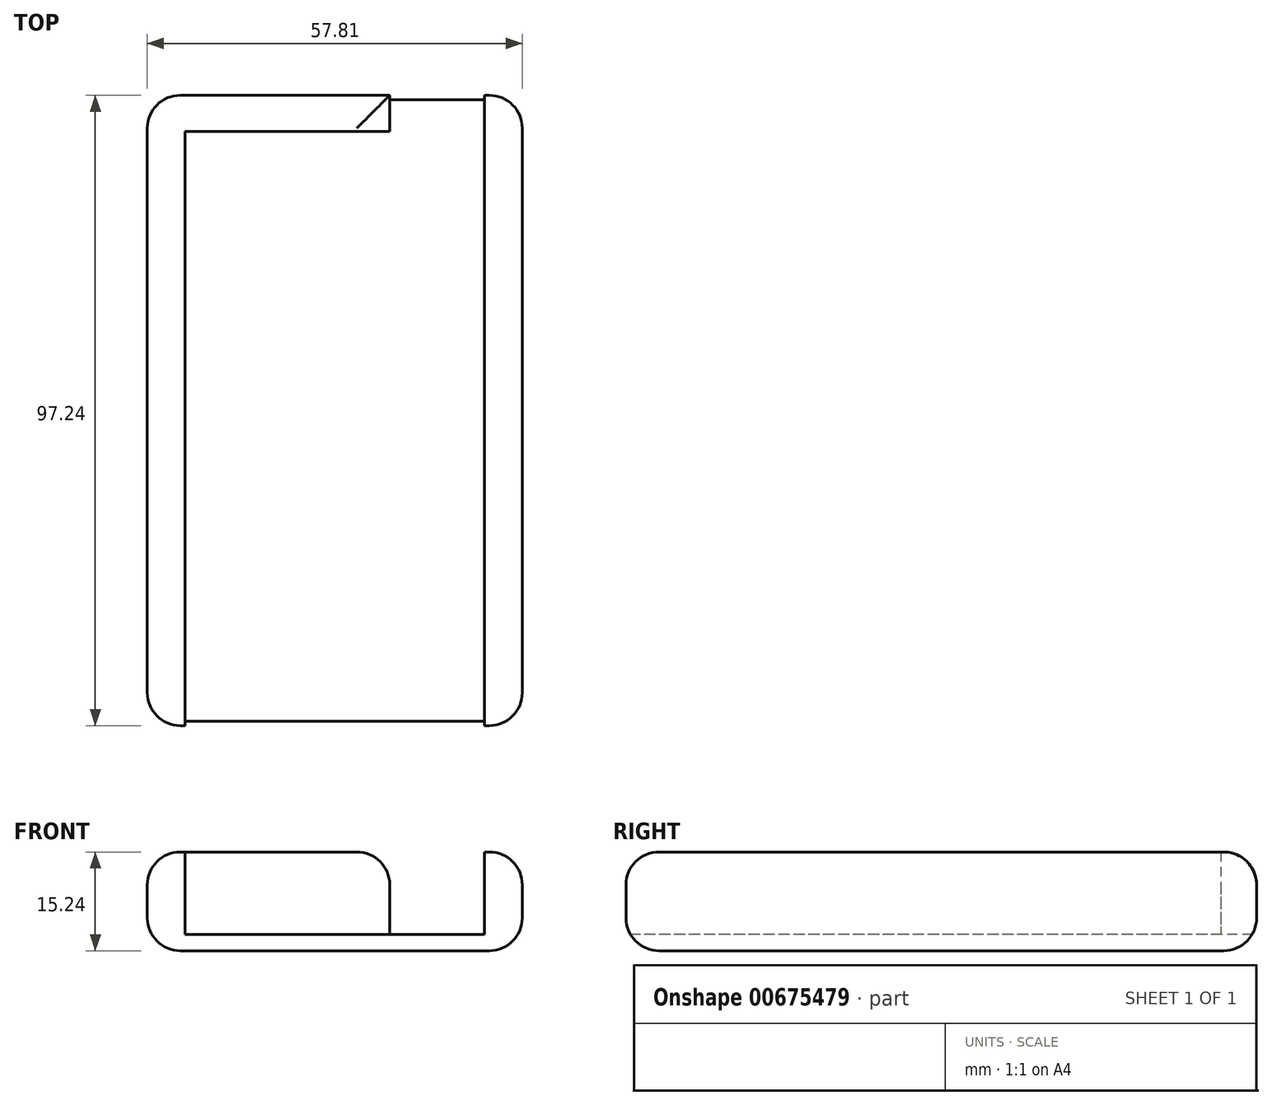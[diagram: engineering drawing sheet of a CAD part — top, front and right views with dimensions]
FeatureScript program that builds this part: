
annotation { "Feature Type Name" : "Feature", "Feature Type Description" : "" }
export const myFeature = defineFeature(function(context is Context, id is Id, definition is map)
    precondition{}
    {
        {
            var Q0;
            Q0=qCreatedBy(makeId("Top.planeOp"),FACE);
            var sketch = newSketch(context, id + "F0", { "sketchPlane" : qUnion([Q0])});
            skLineSegment(sketch, "E0.bottom", {"start": v(-29.05, 48.62) * mm, "end": v(29.05, 48.62) * mm});
            skLineSegment(sketch, "E0.top", {"start": v(-29.05, -48.62) * mm, "end": v(29.05, -48.62) * mm});
            skLineSegment(sketch, "E0.left", {"start": v(-29.05, 48.62) * mm, "end": v(-29.05, -48.62) * mm});
            skLineSegment(sketch, "E0.right", {"start": v(29.05, 48.62) * mm, "end": v(29.05, -48.62) * mm});
            skPoint(sketch, "E0.middle", {"position": v(0, 0) * mm});
            skSolve(sketch);
        }
        {
            var Q0;
            Q0=makeQuery(id+"F0.imprint","IMPRINT",FACE,{"disambiguationData":[TD([[makeQuery(id+"F0.imprint","IMPRINT",EDGE,{"derivedFrom":sQuery(id+"F0.wireOp",EDGE,"E0.bottom")}),-1.0]])]});
            var sketch = newSketch(context, id + "F1", { "sketchPlane" : qUnion([Q0])});
            skLineSegment(sketch, "E1.bottom", {"start": v(-22.92, 48.62) * mm, "end": v(-28.76, 48.62) * mm});
            skLineSegment(sketch, "E1.top", {"start": v(-22.92, -48.91) * mm, "end": v(-28.76, -48.91) * mm});
            skLineSegment(sketch, "E1.left", {"start": v(-22.92, 48.62) * mm, "end": v(-22.92, -48.91) * mm});
            skLineSegment(sketch, "E1.right", {"start": v(-28.76, 48.62) * mm, "end": v(-28.76, -48.91) * mm});
            skLineSegment(sketch, "E2.bottom", {"start": v(29.05, 48.91) * mm, "end": v(23.21, 48.91) * mm});
            skLineSegment(sketch, "E2.top", {"start": v(29.05, -48.91) * mm, "end": v(23.21, -48.91) * mm});
            skLineSegment(sketch, "E2.left", {"start": v(29.05, 48.91) * mm, "end": v(29.05, -48.91) * mm});
            skLineSegment(sketch, "E2.right", {"start": v(23.21, 48.91) * mm, "end": v(23.21, -48.91) * mm});
            skSolve(sketch);
        }
        {
            var Q0;
            Q0=makeQuery(id+"F0.imprint","IMPRINT",FACE,{"disambiguationData":[TD([[makeQuery(id+"F0.imprint","IMPRINT",EDGE,{"derivedFrom":sQuery(id+"F0.wireOp",EDGE,"E0.bottom")}),-1.0]])]});
            extrude(context, id + "F2", {"entities" : qUnion([Q0]), "oppositeDirection" : true, "depth" : 2.54 * mm, "offsetDistance" : 25.4 * mm});
        }
        {
            var Q0;
            {var subQ0=sQuery(id+"F1.wireOp",EDGE,"E2.left");var subQ1=makeQuery(id+"F0.imprint","IMPRINT",EDGE,{"derivedFrom":sQuery(id+"F0.wireOp",EDGE,"E0.bottom")});var subQ2=makeQuery(id+"F1.imprint","INTERSECT",VERTEX,{"derivedFrom":[subQ1,subQ0]});Q0=makeQuery(id+"F1.imprint","IMPRINT",FACE,{"disambiguationData":[TD([[makeQuery(id+"F1.imprint","IMPRINT",EDGE,{"disambiguationData":[TD([[subQ2,-1.0]])],"derivedFrom":subQ0}),-1.0]])]});}
            var Q1;
            {var subQ0=sQuery(id+"F1.wireOp",EDGE,"E1.bottom");Q1=makeQuery(id+"F1.imprint","IMPRINT",FACE,{"disambiguationData":[TD([[makeQuery(id+"F1.imprint","IMPRINT",EDGE,{"derivedFrom":subQ0}),-1.0]])]});}
            extrude(context, id + "F3", {"entities" : qUnion([Q0, Q1]), "operationType" : NewBodyOperationType.ADD, "depth" : 12.7 * mm, "offsetDistance" : 25.4 * mm});
        }
        {
            var Q0;
            Q0=makeQuery(id+"F3.opExtrude","SWEPT_EDGE",EDGE,{"disambiguationData":[OSD([sQuery(id+"F0.wireOp",EDGE,"E0.bottom"),sQuery(id+"F1.wireOp",EDGE,"E1.bottom"),sQuery(id+"F1.wireOp",EDGE,"E1.right")])]});
            var Q1;
            {var subQ0=sQuery(id+"F0.wireOp",EDGE,"E0.bottom");Q1=makeQuery(id+"F3.boolean.opBoolean","MERGE",EDGE,{"derivedFrom":[makeQuery(id+"F2.opExtrude","SWEPT_EDGE",EDGE,{"disambiguationData":[OSD([subQ0,sQuery(id+"F0.wireOp",EDGE,"E0.right")])]}),makeQuery(id+"F3.opExtrude","SWEPT_EDGE",EDGE,{"disambiguationData":[OSD([subQ0,sQuery(id+"F1.wireOp",EDGE,"E2.left")])]})]});}
            var Q2;
            Q2=makeQuery(id+"F3.opExtrude","SWEPT_EDGE",EDGE,{"disambiguationData":[OSD([sQuery(id+"F0.wireOp",EDGE,"E0.top"),sQuery(id+"F1.wireOp",EDGE,"E1.right")])]});
            var Q3;
            {var subQ0=sQuery(id+"F0.wireOp",EDGE,"E0.top");Q3=makeQuery(id+"F3.boolean.opBoolean","MERGE",EDGE,{"derivedFrom":[makeQuery(id+"F2.opExtrude","SWEPT_EDGE",EDGE,{"disambiguationData":[OSD([subQ0,sQuery(id+"F0.wireOp",EDGE,"E0.right")])]}),makeQuery(id+"F3.opExtrude","SWEPT_EDGE",EDGE,{"disambiguationData":[OSD([subQ0,sQuery(id+"F1.wireOp",EDGE,"E2.left")])]})]});}
            fillet(context, id + "F4", {"entities" : qUnion([Q0, Q1, Q2, Q3]), "radius" : 5.08 * mm, "tangentPropagation" : true, "allowEdgeOverflow" : false});
        }
        {
            var Q0;
            Q0=makeQuery(id+"F2.opExtrude","SWEPT_EDGE",EDGE,{"disambiguationData":[OSD([sQuery(id+"F0.wireOp",EDGE,"E0.top"),sQuery(id+"F0.wireOp",EDGE,"E0.left")])]});
            var Q1;
            Q1=makeQuery(id+"F2.opExtrude","SWEPT_EDGE",EDGE,{"disambiguationData":[OSD([sQuery(id+"F0.wireOp",EDGE,"E0.bottom"),sQuery(id+"F0.wireOp",EDGE,"E0.left")])]});
            fillet(context, id + "F5", {"entities" : qUnion([Q0, Q1]), "radius" : 5.08 * mm, "tangentPropagation" : true, "allowEdgeOverflow" : false});
        }
        {
            var Q0;
            Q0=makeQuery(id+"F2.opExtrude","CAP_EDGE",EDGE,{"disambiguationData":[OSD([sQuery(id+"F0.wireOp",EDGE,"E0.right")])],"isStart":false});
            fillet(context, id + "F6", {"entities" : qUnion([Q0]), "radius" : 5.08 * mm, "tangentPropagation" : true, "allowEdgeOverflow" : false});
        }
        {
            var Q0;
            Q0=makeQuery(id+"F3.opExtrude","CAP_EDGE",EDGE,{"disambiguationData":[OSD([sQuery(id+"F1.wireOp",EDGE,"E1.right")])],"isStart":false});
            var Q1;
            Q1=makeQuery(id+"F3.opExtrude","CAP_EDGE",EDGE,{"disambiguationData":[OSD([sQuery(id+"F1.wireOp",EDGE,"E2.left")])],"isStart":false});
            fillet(context, id + "F7", {"entities" : qUnion([Q0, Q1]), "radius" : 5.08 * mm, "tangentPropagation" : true, "allowEdgeOverflow" : false});
        }
        {
            var Q0;
            Q0=qCreatedBy(makeId("Top.planeOp"),FACE);
            var sketch = newSketch(context, id + "F8", { "sketchPlane" : qUnion([Q0])});
            skLineSegment(sketch, "E3.bottom", {"start": v(-22.92, 48.62) * mm, "end": v(8.61, 48.62) * mm});
            skLineSegment(sketch, "E3.top", {"start": v(-22.92, 43.07) * mm, "end": v(8.61, 43.07) * mm});
            skLineSegment(sketch, "E3.left", {"start": v(-22.92, 48.62) * mm, "end": v(-22.92, 43.07) * mm});
            skLineSegment(sketch, "E3.right", {"start": v(8.61, 48.62) * mm, "end": v(8.61, 43.07) * mm});
            skSolve(sketch);
        }
        {
            var Q0;
            Q0 = qSketchRegion(id + "F8", true);
            extrude(context, id + "F9", {"entities" : qUnion([Q0]), "operationType" : NewBodyOperationType.ADD, "depth" : 12.7 * mm, "offsetDistance" : 25.4 * mm});
        }
        {
            var Q0;
            Q0=makeQuery(id+"F9.opExtrude","CAP_EDGE",EDGE,{"disambiguationData":[OSD([sQuery(id+"F8.wireOp",EDGE,"E3.right")])],"isStart":false});
            var Q1;
            Q1=makeQuery(id+"F9.opExtrude","CAP_EDGE",EDGE,{"disambiguationData":[OSD([sQuery(id+"F8.wireOp",EDGE,"E3.bottom")])],"isStart":false});
            var Q2;
            Q2=makeQuery(id+"F9.opExtrude","CAP_EDGE",EDGE,{"disambiguationData":[OSD([sQuery(id+"F8.wireOp",EDGE,"E3.bottom")])],"isStart":true});
            fillet(context, id + "F10", {"entities" : qUnion([Q0, Q1, Q2]), "radius" : 5.08 * mm, "tangentPropagation" : true, "allowEdgeOverflow" : false});
        }
    });
